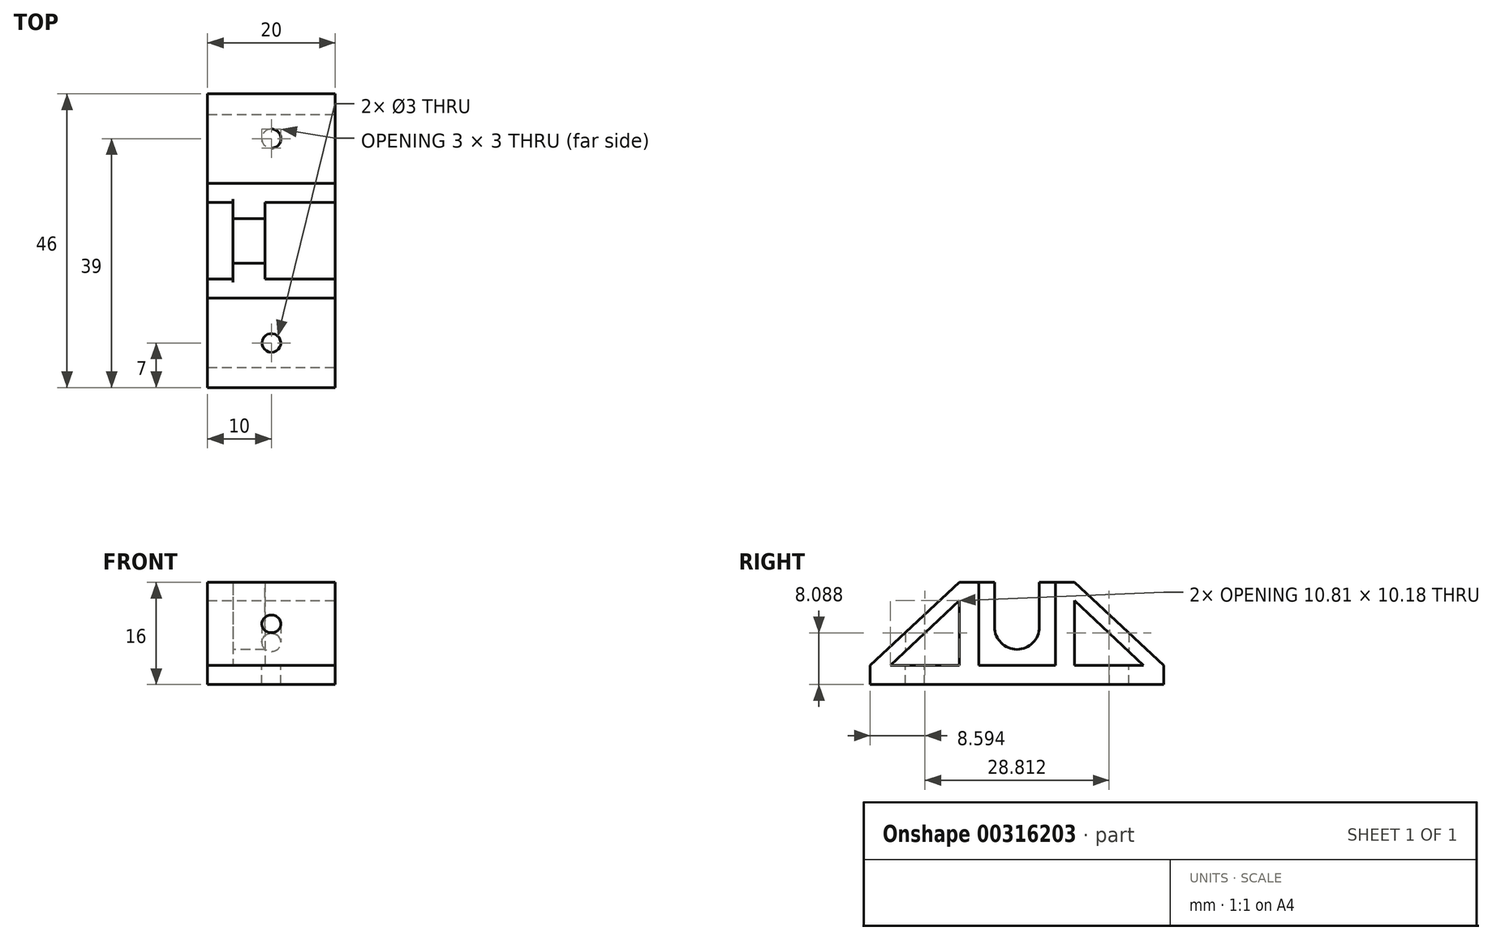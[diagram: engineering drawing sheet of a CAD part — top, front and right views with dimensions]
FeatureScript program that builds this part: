
annotation { "Feature Type Name" : "Feature", "Feature Type Description" : "" }
export const myFeature = defineFeature(function(context is Context, id is Id, definition is map)
    precondition{}
    {
        {
            var Q0;
            Q0=qCreatedBy(makeId("Top.planeOp"),FACE);
            var sketch = newSketch(context, id + "F0", { "sketchPlane" : qUnion([Q0])});
            skLineSegment(sketch, "E0.bottom", {"start": v(0, 0) * mm, "end": v(20, 0) * mm});
            skLineSegment(sketch, "E0.top", {"start": v(0, -46) * mm, "end": v(20, -46) * mm});
            skLineSegment(sketch, "E0.left", {"start": v(0, 0) * mm, "end": v(0, -46) * mm});
            skLineSegment(sketch, "E0.right", {"start": v(20, 0) * mm, "end": v(20, -46) * mm});
            skSolve(sketch);
        }
        {
            var Q0;
            Q0=makeQuery(id+"F0.imprint","IMPRINT",FACE,{"disambiguationData":[TD([[makeQuery(id+"F0.imprint","IMPRINT",EDGE,{"derivedFrom":sQuery(id+"F0.wireOp",EDGE,"E0.bottom")}),-1.0]])]});
            extrude(context, id + "F1", {"entities" : qUnion([Q0]), "depth" : 3 * mm});
        }
        {
            var Q0;
            Q0=makeQuery(id+"F1.opExtrude","CAP_FACE",FACE,{"disambiguationData":[OSD([sQuery(id+"F0.wireOp",EDGE,"E0.bottom"),sQuery(id+"F0.wireOp",EDGE,"E0.top"),sQuery(id+"F0.wireOp",EDGE,"E0.left"),sQuery(id+"F0.wireOp",EDGE,"E0.right")])],"isStart":false});
            var sketch = newSketch(context, id + "F2", { "sketchPlane" : qUnion([Q0])});
            skLineSegment(sketch, "E1.bottom", {"start": v(0, 0) * mm, "end": v(20, 0) * mm});
            skLineSegment(sketch, "E1.top", {"start": v(0, -14) * mm, "end": v(20, -14) * mm});
            skLineSegment(sketch, "E1.left", {"start": v(0, 0) * mm, "end": v(0, -14) * mm});
            skLineSegment(sketch, "E1.right", {"start": v(20, 0) * mm, "end": v(20, -14) * mm});
            skLineSegment(sketch, "E2.top", {"start": v(0, -17) * mm, "end": v(20, -17) * mm});
            skLineSegment(sketch, "E2.left", {"start": v(0, -14) * mm, "end": v(0, -17) * mm});
            skLineSegment(sketch, "E2.right", {"start": v(20, -14) * mm, "end": v(20, -17) * mm});
            skLineSegment(sketch, "E3.top", {"start": v(0, -29) * mm, "end": v(20, -29) * mm});
            skLineSegment(sketch, "E3.left", {"start": v(0, -17) * mm, "end": v(0, -29) * mm});
            skLineSegment(sketch, "E3.right", {"start": v(20, -17) * mm, "end": v(20, -29) * mm});
            skLineSegment(sketch, "E4.top", {"start": v(0, -32) * mm, "end": v(20, -32) * mm});
            skLineSegment(sketch, "E4.left", {"start": v(0, -29) * mm, "end": v(0, -32) * mm});
            skLineSegment(sketch, "E4.right", {"start": v(20, -29) * mm, "end": v(20, -32) * mm});
            skSolve(sketch);
        }
        {
            var Q0;
            Q0=makeQuery(id+"F2.imprint","IMPRINT",FACE,{"disambiguationData":[TD([[makeQuery(id+"F2.imprint","IMPRINT",EDGE,{"derivedFrom":sQuery(id+"F2.wireOp",EDGE,"E1.top")}),-1.0]])]});
            var Q1;
            Q1=makeQuery(id+"F2.imprint","IMPRINT",FACE,{"disambiguationData":[TD([[makeQuery(id+"F2.imprint","IMPRINT",EDGE,{"derivedFrom":sQuery(id+"F2.wireOp",EDGE,"E3.top")}),-1.0]])]});
            extrude(context, id + "F3", {"entities" : qUnion([Q0, Q1]), "operationType" : NewBodyOperationType.ADD, "depth" : 13 * mm});
        }
        {
            var Q0;
            {var subQ0=sQuery(id+"F0.wireOp",EDGE,"E0.left");var subQ1=sQuery(id+"F0.wireOp",EDGE,"E0.right");var subQ2=sQuery(id+"F0.wireOp",EDGE,"E0.top");Q0=makeQuery(id+"F3.boolean.opBoolean","SPLIT",FACE,{"disambiguationData":[TD([makeQuery(id+"F1.opExtrude","SWEPT_FACE",FACE,{"disambiguationData":[OSD([subQ2])]})])],"derivedFrom":makeQuery(id+"F1.opExtrude","CAP_FACE",FACE,{"disambiguationData":[OSD([sQuery(id+"F0.wireOp",EDGE,"E0.bottom"),subQ2,subQ0,subQ1])],"isStart":false})});}
            var sketch = newSketch(context, id + "F4", { "sketchPlane" : qUnion([Q0])});
            skSolve(sketch);
        }
        {
            var Q0;
            {var subQ0=sQuery(id+"F0.wireOp",EDGE,"E0.top");Q0=makeQuery(id+"F4.imprint","IMPRINT",FACE,{"disambiguationData":[TD([[makeQuery(id+"F4.imprint","IMPRINT",EDGE,{"derivedFrom":makeQuery(id+"F1.opExtrude","CAP_EDGE",EDGE,{"disambiguationData":[OSD([subQ0])],"isStart":false})}),1.0]])]});}
            var sketch = newSketch(context, id + "F5", { "sketchPlane" : qUnion([Q0])});
            skLineSegment(sketch, "E5.bottom", {"start": v(0, 0) * mm, "end": v(10, 0) * mm});
            skLineSegment(sketch, "E5.top", {"start": v(0, -7) * mm, "end": v(10, -7) * mm});
            skLineSegment(sketch, "E5.left", {"start": v(0, 0) * mm, "end": v(0, -7) * mm});
            skLineSegment(sketch, "E5.right", {"start": v(10, 0) * mm, "end": v(10, -7) * mm});
            skCircle(sketch, "E6", {"center": v(10, -7) * mm, "radius": 1.5 * mm});
            skLineSegment(sketch, "E7.top", {"start": v(0, -39) * mm, "end": v(10, -39) * mm});
            skLineSegment(sketch, "E7.left", {"start": v(0, -7) * mm, "end": v(0, -39) * mm});
            skLineSegment(sketch, "E7.right", {"start": v(10, -7) * mm, "end": v(10, -39) * mm});
            skCircle(sketch, "E8", {"center": v(10, -39) * mm, "radius": 1.5 * mm});
            skSolve(sketch);
        }
        {
            var Q0;
            {var subQ0=sQuery(id+"F5.wireOp",EDGE,"E7.right");var subQ1=sQuery(id+"F5.wireOp",EDGE,"E7.top");var subQ2=makeQuery(id+"F5.imprint","INTERSECT",VERTEX,{"derivedFrom":[subQ1,subQ0]});Q0=makeQuery(id+"F5.imprint","IMPRINT",FACE,{"disambiguationData":[TD([[makeQuery(id+"F5.imprint","IMPRINT",EDGE,{"disambiguationData":[TD([[subQ2,1.0]])],"derivedFrom":subQ1}),-1.0]])]});}
            var Q1;
            {var subQ0=sQuery(id+"F5.wireOp",EDGE,"E7.right");var subQ1=sQuery(id+"F5.wireOp",EDGE,"E7.top");var subQ2=makeQuery(id+"F5.imprint","INTERSECT",VERTEX,{"derivedFrom":[subQ1,subQ0]});Q1=makeQuery(id+"F5.imprint","IMPRINT",FACE,{"disambiguationData":[TD([[makeQuery(id+"F5.imprint","IMPRINT",EDGE,{"disambiguationData":[TD([[subQ2,1.0]])],"derivedFrom":subQ1}),1.0]])]});}
            extrude(context, id + "F6", {"entities" : qUnion([Q0, Q1]), "operationType" : NewBodyOperationType.REMOVE, "oppositeDirection" : true, "depth" : 25 * mm});
        }
        {
            var Q0;
            {var subQ1=sQuery(id+"F5.wireOp",EDGE,"E5.right");var subQ3=sQuery(id+"F5.wireOp",EDGE,"E6");var subQ4=makeQuery(id+"F5.imprint","INTERSECT",VERTEX,{"derivedFrom":[subQ1,subQ3]});Q0=makeQuery(id+"F5.imprint","IMPRINT",FACE,{"disambiguationData":[TD([[makeQuery(id+"F5.imprint","IMPRINT",EDGE,{"disambiguationData":[TD([[subQ4,1.0]])],"derivedFrom":subQ3}),1.0]])]});}
            var Q1;
            {var subQ0=sQuery(id+"F5.wireOp",EDGE,"E7.right");var subQ1=sQuery(id+"F5.wireOp",EDGE,"E6");var subQ2=makeQuery(id+"F5.imprint","INTERSECT",VERTEX,{"derivedFrom":[subQ1,subQ0]});Q1=makeQuery(id+"F5.imprint","IMPRINT",FACE,{"disambiguationData":[TD([[makeQuery(id+"F5.imprint","IMPRINT",EDGE,{"disambiguationData":[TD([[subQ2,1.0]])],"derivedFrom":subQ1}),1.0]])]});}
            var Q2;
            {var subQ1=sQuery(id+"F5.wireOp",EDGE,"E5.right");var subQ3=sQuery(id+"F5.wireOp",EDGE,"E6");var subQ4=makeQuery(id+"F5.imprint","INTERSECT",VERTEX,{"derivedFrom":[subQ1,subQ3]});Q2=makeQuery(id+"F5.imprint","IMPRINT",FACE,{"disambiguationData":[TD([[makeQuery(id+"F5.imprint","IMPRINT",EDGE,{"disambiguationData":[TD([[subQ4,-1.0]])],"derivedFrom":subQ3}),1.0]])]});}
            extrude(context, id + "F7", {"entities" : qUnion([Q0, Q1, Q2]), "operationType" : NewBodyOperationType.REMOVE, "oppositeDirection" : true, "depth" : 25 * mm});
        }
        {
            var Q0;
            Q0=makeQuery(id+"F3.boolean.opBoolean","MERGE",FACE,{"derivedFrom":[makeQuery(id+"F1.opExtrude","SWEPT_FACE",FACE,{"disambiguationData":[OSD([sQuery(id+"F0.wireOp",EDGE,"E0.left")])]}),makeQuery(id+"F3.opExtrude","SWEPT_FACE",FACE,{"disambiguationData":[OSD([sQuery(id+"F2.wireOp",EDGE,"E2.left")])]}),makeQuery(id+"F3.opExtrude","SWEPT_FACE",FACE,{"disambiguationData":[OSD([sQuery(id+"F2.wireOp",EDGE,"E4.left")])]})]});
            var sketch = newSketch(context, id + "F8", { "sketchPlane" : qUnion([Q0])});
            skLineSegment(sketch, "E9", {"start": v(32, 16) * mm, "end": v(46, 3) * mm});
            skLineSegment(sketch, "E10", {"start": v(46, 3) * mm, "end": v(46, 0) * mm});
            skLineSegment(sketch, "E11", {"start": v(46, 0) * mm, "end": v(29, 16) * mm});
            skLineSegment(sketch, "E12", {"start": v(29, 16) * mm, "end": v(32, 16) * mm});
            skSolve(sketch);
        }
        {
            var Q0;
            Q0 = qSketchRegion(id + "F8", true);
            extrude(context, id + "F9", {"entities" : qUnion([Q0]), "operationType" : NewBodyOperationType.ADD, "oppositeDirection" : true, "depth" : 20 * mm});
        }
        {
            var Q0;
            Q0=makeQuery(id+"F9.boolean.opBoolean","MERGE",FACE,{"derivedFrom":[makeQuery(id+"F3.boolean.opBoolean","MERGE",FACE,{"derivedFrom":[makeQuery(id+"F1.opExtrude","SWEPT_FACE",FACE,{"disambiguationData":[OSD([sQuery(id+"F0.wireOp",EDGE,"E0.right")])]}),makeQuery(id+"F3.opExtrude","SWEPT_FACE",FACE,{"disambiguationData":[OSD([sQuery(id+"F2.wireOp",EDGE,"E2.right")])]}),makeQuery(id+"F3.opExtrude","SWEPT_FACE",FACE,{"disambiguationData":[OSD([sQuery(id+"F2.wireOp",EDGE,"E4.right")])]})]}),makeQuery(id+"F9.opExtrude","CAP_FACE",FACE,{"disambiguationData":[OSD([sQuery(id+"F8.wireOp",EDGE,"E9"),sQuery(id+"F8.wireOp",EDGE,"E10"),sQuery(id+"F8.wireOp",EDGE,"E11"),sQuery(id+"F8.wireOp",EDGE,"E12")])],"isStart":false})]});
            var sketch = newSketch(context, id + "F10", { "sketchPlane" : qUnion([Q0])});
            skLineSegment(sketch, "E13", {"start": v(-14, 16) * mm, "end": v(0, 3) * mm});
            skLineSegment(sketch, "E14", {"start": v(0, 3) * mm, "end": v(0, 0) * mm});
            skLineSegment(sketch, "E15", {"start": v(0, 0) * mm, "end": v(-17, 16) * mm});
            skLineSegment(sketch, "E16", {"start": v(-17, 16) * mm, "end": v(-14, 16) * mm});
            skSolve(sketch);
        }
        {
            var Q0;
            {var subQ0=sQuery(id+"F10.wireOp",EDGE,"E13");Q0=makeQuery(id+"F10.imprint","IMPRINT",FACE,{"disambiguationData":[TD([[makeQuery(id+"F10.imprint","IMPRINT",EDGE,{"derivedFrom":subQ0}),-1.0]])]});}
            extrude(context, id + "F11", {"entities" : qUnion([Q0]), "operationType" : NewBodyOperationType.ADD, "oppositeDirection" : true, "depth" : 20 * mm});
        }
        {
            var Q0;
            {var subQ0=sQuery(id+"F5.wireOp",EDGE,"E7.right");var subQ1=sQuery(id+"F5.wireOp",EDGE,"E7.top");var subQ2=makeQuery(id+"F5.imprint","INTERSECT",VERTEX,{"derivedFrom":[subQ1,subQ0]});Q0=makeQuery(id+"F5.imprint","IMPRINT",FACE,{"disambiguationData":[TD([[makeQuery(id+"F5.imprint","IMPRINT",EDGE,{"disambiguationData":[TD([[subQ2,1.0]])],"derivedFrom":subQ1}),-1.0]])]});}
            var Q1;
            {var subQ0=sQuery(id+"F5.wireOp",EDGE,"E7.right");var subQ1=sQuery(id+"F5.wireOp",EDGE,"E7.top");var subQ2=makeQuery(id+"F5.imprint","INTERSECT",VERTEX,{"derivedFrom":[subQ1,subQ0]});Q1=makeQuery(id+"F5.imprint","IMPRINT",FACE,{"disambiguationData":[TD([[makeQuery(id+"F5.imprint","IMPRINT",EDGE,{"disambiguationData":[TD([[subQ2,1.0]])],"derivedFrom":subQ1}),1.0]])]});}
            extrude(context, id + "F12", {"entities" : qUnion([Q0, Q1]), "operationType" : NewBodyOperationType.REMOVE, "depth" : 25 * mm});
        }
        {
            var Q0;
            {var subQ1=sQuery(id+"F5.wireOp",EDGE,"E5.right");var subQ3=sQuery(id+"F5.wireOp",EDGE,"E6");var subQ4=makeQuery(id+"F5.imprint","INTERSECT",VERTEX,{"derivedFrom":[subQ1,subQ3]});Q0=makeQuery(id+"F5.imprint","IMPRINT",FACE,{"disambiguationData":[TD([[makeQuery(id+"F5.imprint","IMPRINT",EDGE,{"disambiguationData":[TD([[subQ4,1.0]])],"derivedFrom":subQ3}),1.0]])]});}
            var Q1;
            {var subQ0=sQuery(id+"F5.wireOp",EDGE,"E7.right");var subQ1=sQuery(id+"F5.wireOp",EDGE,"E6");var subQ2=makeQuery(id+"F5.imprint","INTERSECT",VERTEX,{"derivedFrom":[subQ1,subQ0]});Q1=makeQuery(id+"F5.imprint","IMPRINT",FACE,{"disambiguationData":[TD([[makeQuery(id+"F5.imprint","IMPRINT",EDGE,{"disambiguationData":[TD([[subQ2,1.0]])],"derivedFrom":subQ1}),1.0]])]});}
            var Q2;
            {var subQ1=sQuery(id+"F5.wireOp",EDGE,"E5.right");var subQ3=sQuery(id+"F5.wireOp",EDGE,"E6");var subQ4=makeQuery(id+"F5.imprint","INTERSECT",VERTEX,{"derivedFrom":[subQ1,subQ3]});Q2=makeQuery(id+"F5.imprint","IMPRINT",FACE,{"disambiguationData":[TD([[makeQuery(id+"F5.imprint","IMPRINT",EDGE,{"disambiguationData":[TD([[subQ4,-1.0]])],"derivedFrom":subQ3}),1.0]])]});}
            extrude(context, id + "F13", {"entities" : qUnion([Q0, Q1, Q2]), "operationType" : NewBodyOperationType.REMOVE, "depth" : 25 * mm});
        }
        {
            var Q0;
            {var subQ0=sQuery(id+"F5.wireOp",EDGE,"E7.right");var subQ1=sQuery(id+"F5.wireOp",EDGE,"E6");var subQ2=makeQuery(id+"F5.imprint","INTERSECT",VERTEX,{"derivedFrom":[subQ1,subQ0]});Q0=makeQuery(id+"F5.imprint","IMPRINT",FACE,{"disambiguationData":[TD([[makeQuery(id+"F5.imprint","IMPRINT",EDGE,{"disambiguationData":[TD([[subQ2,1.0]])],"derivedFrom":subQ1}),-1.0]])]});}
            var sketch = newSketch(context, id + "F14", { "sketchPlane" : qUnion([Q0])});
            skLineSegment(sketch, "E17.bottom", {"start": v(0, 0) * mm, "end": v(4, 0) * mm});
            skLineSegment(sketch, "E17.top", {"start": v(0, -17) * mm, "end": v(4, -17) * mm});
            skLineSegment(sketch, "E17.left", {"start": v(0, 0) * mm, "end": v(0, -17) * mm});
            skLineSegment(sketch, "E17.right", {"start": v(4, 0) * mm, "end": v(4, -17) * mm});
            skLineSegment(sketch, "E18.bottom", {"start": v(4, -17) * mm, "end": v(9, -17) * mm});
            skLineSegment(sketch, "E18.top", {"start": v(4, -29) * mm, "end": v(9, -29) * mm});
            skLineSegment(sketch, "E18.left", {"start": v(4, -17) * mm, "end": v(4, -29) * mm});
            skLineSegment(sketch, "E18.right", {"start": v(9, -17) * mm, "end": v(9, -29) * mm});
            skSolve(sketch);
        }
        {
            var Q0;
            Q0=makeQuery(id+"F14.imprint","IMPRINT",FACE,{"disambiguationData":[TD([[makeQuery(id+"F14.imprint","IMPRINT",EDGE,{"derivedFrom":sQuery(id+"F14.wireOp",EDGE,"E18.bottom")}),-1.0]])]});
            extrude(context, id + "F15", {"entities" : qUnion([Q0]), "operationType" : NewBodyOperationType.ADD, "depth" : 13 * mm});
        }
        {
            var Q0;
            Q0=makeQuery(id+"F15.opExtrude","SWEPT_FACE",FACE,{"disambiguationData":[OSD([sQuery(id+"F14.wireOp",EDGE,"E18.left")])]});
            var sketch = newSketch(context, id + "F16", { "sketchPlane" : qUnion([Q0])});
            skLineSegment(sketch, "E19.bottom", {"start": v(17, 3) * mm, "end": v(23, 3) * mm});
            skLineSegment(sketch, "E19.top", {"start": v(17, 9) * mm, "end": v(23, 9) * mm});
            skLineSegment(sketch, "E19.left", {"start": v(17, 3) * mm, "end": v(17, 9) * mm});
            skLineSegment(sketch, "E19.right", {"start": v(23, 3) * mm, "end": v(23, 9) * mm});
            skCircle(sketch, "E20", {"center": v(23, 9) * mm, "radius": 3.5 * mm});
            skLineSegment(sketch, "E21", {"start": v(26.5, 9) * mm, "end": v(26.5, 16) * mm});
            skPoint(sketch, "E22.oppositeSnap0", {"position": v(20, 9) * mm});
            skLineSegment(sketch, "E22.bottom", {"start": v(26.5, 16) * mm, "end": v(19.5, 16) * mm});
            skLineSegment(sketch, "E22.top", {"start": v(26.5, 9) * mm, "end": v(19.5, 9) * mm});
            skLineSegment(sketch, "E22.left", {"start": v(26.5, 16) * mm, "end": v(26.5, 9) * mm});
            skLineSegment(sketch, "E22.right", {"start": v(19.5, 16) * mm, "end": v(19.5, 9) * mm});
            skSolve(sketch);
        }
        {
            var Q0;
            Q0=makeQuery(id+"F16.imprint","IMPRINT",FACE,{"disambiguationData":[TD([[makeQuery(id+"F16.imprint","IMPRINT",EDGE,{"derivedFrom":sQuery(id+"F16.wireOp",EDGE,"E22.bottom")}),-1.0]])]});
            var Q1;
            {var subQ0=sQuery(id+"F16.wireOp",EDGE,"E22.top");var subQ4=makeQuery(id+"F16.imprint","INTERSECT",VERTEX,{"derivedFrom":[sQuery(id+"F16.wireOp",EDGE,"E19.right"),subQ0]});Q1=makeQuery(id+"F16.imprint","IMPRINT",FACE,{"disambiguationData":[TD([[makeQuery(id+"F16.imprint","IMPRINT",EDGE,{"disambiguationData":[TD([[subQ4,1.0]])],"derivedFrom":subQ0}),-1.0]])]});}
            var Q2;
            {var subQ0=sQuery(id+"F16.wireOp",EDGE,"E22.top");var subQ1=sQuery(id+"F16.wireOp",EDGE,"E19.right");var subQ2=makeQuery(id+"F16.imprint","INTERSECT",VERTEX,{"derivedFrom":[subQ1,subQ0]});Q2=makeQuery(id+"F16.imprint","IMPRINT",FACE,{"disambiguationData":[TD([[makeQuery(id+"F16.imprint","IMPRINT",EDGE,{"disambiguationData":[TD([[subQ2,1.0]])],"derivedFrom":subQ1}),1.0]])]});}
            var Q3;
            {var subQ0=sQuery(id+"F16.wireOp",EDGE,"E22.top");var subQ1=sQuery(id+"F16.wireOp",EDGE,"E19.right");var subQ2=makeQuery(id+"F16.imprint","INTERSECT",VERTEX,{"derivedFrom":[subQ1,subQ0]});Q3=makeQuery(id+"F16.imprint","IMPRINT",FACE,{"disambiguationData":[TD([[makeQuery(id+"F16.imprint","IMPRINT",EDGE,{"disambiguationData":[TD([[subQ2,1.0]])],"derivedFrom":subQ1}),-1.0]])]});}
            extrude(context, id + "F17", {"entities" : qUnion([Q0, Q1, Q2, Q3]), "operationType" : NewBodyOperationType.REMOVE, "oppositeDirection" : true, "depth" : 25 * mm});
        }
        {
            var Q0;
            {var subQ0=sQuery(id+"F2.wireOp",EDGE,"E2.top");Q0=makeQuery(id+"F15.boolean.opBoolean","SPLIT",EDGE,{"disambiguationData":[TD([makeQuery(id+"F1.opExtrude","SWEPT_FACE",FACE,{"disambiguationData":[OSD([sQuery(id+"F0.wireOp",EDGE,"E0.left")])]})])],"derivedFrom":makeQuery(id+"F3.opExtrude","CAP_EDGE",EDGE,{"disambiguationData":[OSD([subQ0])],"isStart":false})});}
            var Q1;
            {var subQ3=sQuery(id+"F2.wireOp",EDGE,"E3.top");Q1=makeQuery(id+"F15.boolean.opBoolean","SPLIT",EDGE,{"disambiguationData":[TD([makeQuery(id+"F1.opExtrude","SWEPT_FACE",FACE,{"disambiguationData":[OSD([sQuery(id+"F0.wireOp",EDGE,"E0.left")])]})])],"derivedFrom":makeQuery(id+"F3.opExtrude","CAP_EDGE",EDGE,{"disambiguationData":[OSD([subQ3])],"isStart":false})});}
            fillet(context, id + "F18", {"entities" : qUnion([Q0, Q1]), "radius" : 0.5 * mm, "tangentPropagation" : true, "allowEdgeOverflow" : false});
        }
    });
